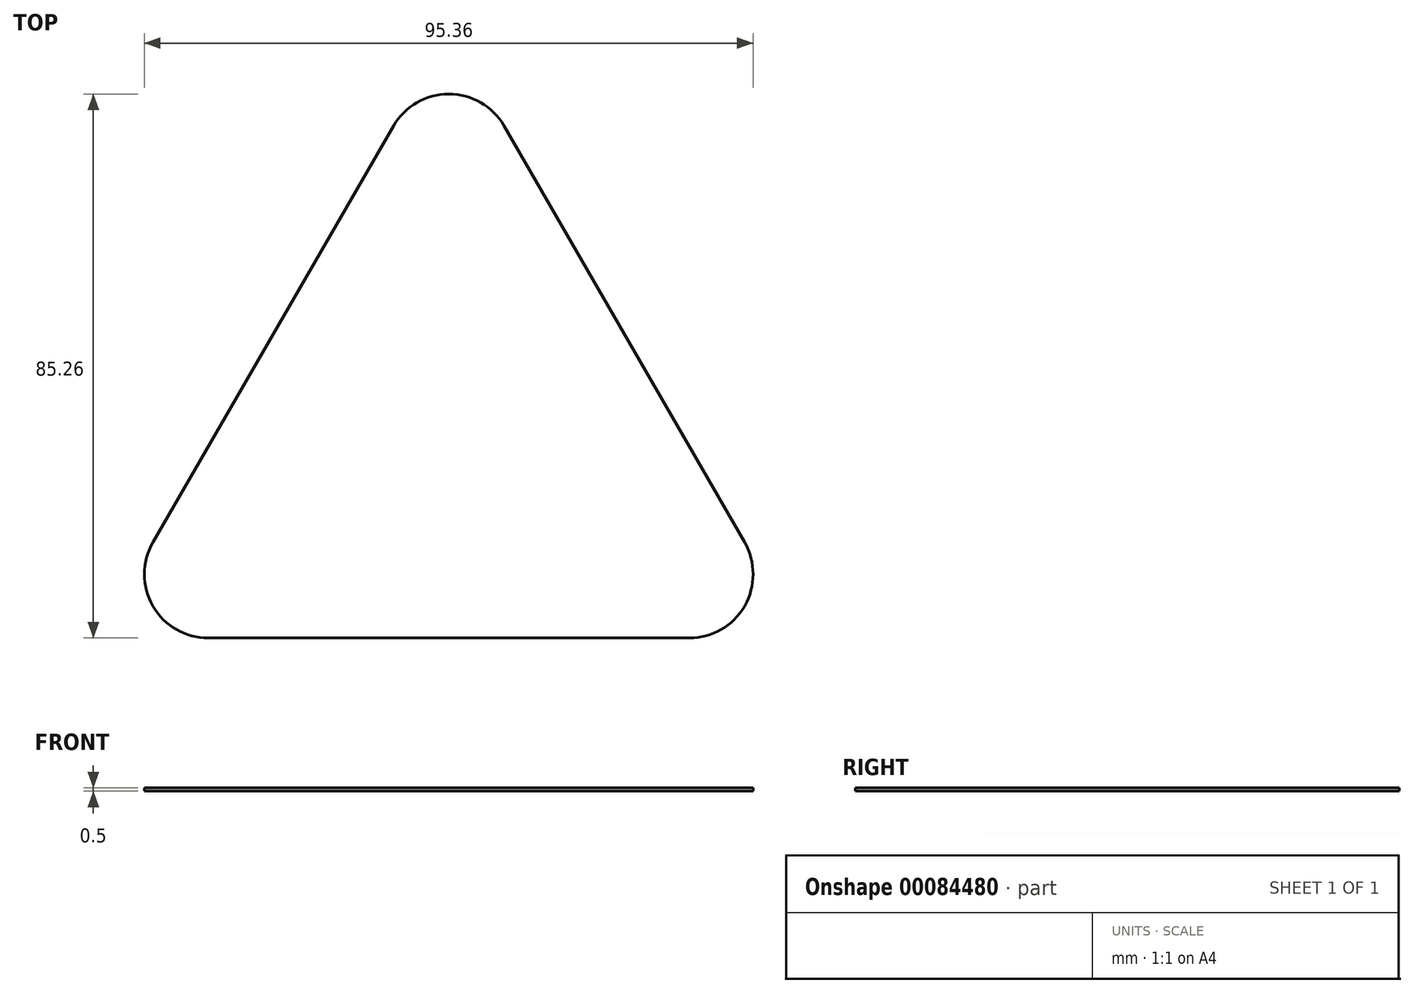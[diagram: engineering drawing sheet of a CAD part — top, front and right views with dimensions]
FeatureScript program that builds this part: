
annotation { "Feature Type Name" : "Feature", "Feature Type Description" : "" }
export const myFeature = defineFeature(function(context is Context, id is Id, definition is map)
    precondition{}
    {
        {
            var Q0;
            Q0=qCreatedBy(makeId("Top.planeOp"),FACE);
            var sketch = newSketch(context, id + "F0", { "sketchPlane" : qUnion([Q0])});
            skLineSegment(sketch, "E0", {"start": v(37.68, 0) * mm, "end": v(-37.68, 0) * mm});
            skLineSegment(sketch, "E1", {"start": v(46.34, 15) * mm, "end": v(8.66, 80.26) * mm});
            skLineSegment(sketch, "E2", {"start": v(-8.66, 80.26) * mm, "end": v(-46.34, 15) * mm});
            skPoint(sketch, "E3.visualSharp", {"position": v(0, 95.26) * mm});
            skArc(sketch, "E3.filletArc", {"start": v(8.66, 80.26) * mm, "mid": v(0, 85.26) * mm, "end": v(-8.66, 80.26) * mm});
            skPoint(sketch, "E4.visualSharp", {"position": v(-55, 0) * mm});
            skArc(sketch, "E4.filletArc", {"start": v(-46.34, 15) * mm, "mid": v(-46.34, 5) * mm, "end": v(-37.68, 0) * mm});
            skPoint(sketch, "E5.visualSharp", {"position": v(55, 0) * mm});
            skArc(sketch, "E5.filletArc", {"start": v(37.68, 0) * mm, "mid": v(46.34, 5) * mm, "end": v(46.34, 15) * mm});
            skSolve(sketch);
        }
        {
            var Q0;
            Q0=qSketchRegion(id+"F0",true);
            extrude(context, id + "F1", {"entities" : qUnion([Q0]), "depth" : 0.5 * mm});
        }
    });
